# Revit family: R-CVA-0001
name_source: partatom
category: Fenêtres
units: mm (PartAtom-declared; Revit-internal decimal feet)

## family parameters
Couper avec des vides une fois chargée = Non
Hôte = Mur
Partagée = Non
Point de calcul de pièce = Non
Toujours verticalement = Oui

## types (2) — shared parameters
Acoustique = Rw (C ; Ctr) = 37 (-1 ; -3) dB
Anti-Effraction = RESISTANCE AUX CHOCS : 2B2 (900J) (selon NF EN 12600))
Applique = Non
Construction analytique = <Aucun>
Description = Chassis vitré, EW30, 37(-1; -3) dB (performance du vitrage), résistance aux chocs 2B2, sans résistance aux UV, avec parcloses bois, sur cadre bois
Fabricant = MONTIBERT
Fiche_Produit = CVA-0001
Huisserie_Delardage Largeur = 8 mm  [stored 0.0262467 ft]
Huisserie_Délardage Bas Epaisseur = 8 mm  [stored 0.0262467 ft]
Huisserie_Délardage Haut  Epaisseur = 8 mm  [stored 0.0262467 ft]
Huisserie_Délardage_Bas = Non
Huisserie_Délardage_Haut = Non
Huisserie_Feuillure Largeur = 24 mm  [stored 0.0787402 ft]
Huisserie_Feuillure_Basse = Non
Huisserie_Feuillure_Haute = Non
Huisserie_Feuillure_Sans = Oui
Huisserie_Matériau = Hêtre
Huisserie_Profil_Epaisseur = 118 mm  [stored 0.387139 ft]
Huisserie_Rainure à Brique_Largeur = 8 mm  [stored 0.0262467 ft]
Materiaux_Dominant = Bois
Modèle = 05 - Châssis Vitré
Montant_1 = Non
Montant_2 = Non
Montant_Largeur = 72 mm  [stored 0.23622 ft]
Note d'identification = CHASSIS VITRE EW30
Parclosage à Recouvrement = Non
Parclose Jeu Epaisseur = 1 mm  [stored 0.00328084 ft]
Parclose Largeur = 24 mm  [stored 0.0787402 ft]
Parclose Recouvrement Epaisseur = 6 mm  [stored 0.019685 ft]
Parclose Recouvrement Largeur = 6 mm  [stored 0.019685 ft]
Parcloses_Matériau = Hêtre
Profil 1_Largeur = 50 mm  [stored 0.164042 ft]
Profil 1_Latéral = Non
Profil 2_Largeur = 50 mm  [stored 0.164042 ft]
Profil 2_Latéral = Non
Profil Bas = Non
Profil Bas_Largeur = 70 mm  [stored 0.229659 ft]
Profil Haut = Non
Profil Haut_Largeur = 50 mm  [stored 0.164042 ft]
Profil_Délardage_Bas_Epaisseur = 8 mm  [stored 0.0262467 ft]
Profil_Délardage_Haut_Epaisseur = 8 mm  [stored 0.0262467 ft]
Profil_Délardage_Largeur = 8 mm  [stored 0.0262467 ft]
Profil_Matériau = Hêtre
Profil_Rainure à Brique_ coté Int = Oui
Profils_Délardage Bas_coté Ext = Non
Profils_Délardage Bas_coté Int = Non
Profils_Délardage Haut_coté Ext = Non
Profils_Délardage Haut_coté Int = Non
Profils_Déplacement X = 8 mm  [stored 0.0262467 ft]
Profils_Déplacement Y' = 8 mm  [stored 0.0262467 ft]
Reference_Commerciale = C EW30 VAc
Resistance_Feu = E30-EW130
Sens_Feu = Recto / Verso
URL = https://www.malerba.fr
Vitrage_Matériau = Verre
zero-valued in all types: Ambrasure, Jeu Bas, Jeu Haut, Jeu Latéral 1, Jeu Latéral 2, Parclose Jeu Largeur, Profils_Déplacement X', Profils_Déplacement Y, X3'_Déduction Délardages Profils, X3_Déduction Délardages Profils, X_Ambrasure, X_Huisserie Décalage Hauteur, X_Huisserie Décalage Hauteur_INV, X_Huisserie Décalage Largeur, X_Huisserie Décalage Largeur_INV, X_Profil 1_Largeur, X_Profil 2_Largeur, X_Profil Bas_Largeur, X_Profil Haut_Largeur

## per-type parameters (varying)
- CVA-0001: Châssis Hauteur Hors Tout=577 mm; Châssis Largeur Hors Tout=1141 mm  [stored 3.74344 ft]; Code_MAJ=2022012506CVA0001; Huisserie_Feuillure Epaisseur=33 mm  [stored 0.108268 ft]; Huisserie_Profil_Largeur=58 mm; Huisserie_Rainure à Brique=Oui; Profil_Déplacement Vers Nu Ext=Oui; Profil_Déplacement Vers Nu Int=Non; Profil_Déplacement Vers l'Huisserie=Non; Profil_Déplacement Vers le Mur=Oui; Profil_Rainure à Brique_ coté Ext=Oui; Recouvrement=Oui; Tunnel=Non; Vitrage Epaisseur=11 mm  [stored 0.0360892 ft]; X1'_Tunnel=577 mm; X1_Tunnel=1141 mm  [stored 3.74344 ft]; X2'_Recouvrement et Applique=561 mm  [stored 1.84055 ft]; X2_Recouvrement et Applique=1125 mm  [stored 3.69094 ft]; X4'_Déduction Délardages Huisseries=16 mm  [stored 0.0524934 ft]; X4_Déduction Délardages Huisseries=16 mm  [stored 0.0524934 ft]; X_Ambrasure Décalage Epaisseur=0 mm  [stored 0 ft]; X_Huisserie_Delardage Largeur=8 mm  [stored 0.0262467 ft]; X_Ouvertur Mur Largeur=1125 mm  [stored 3.69094 ft]; X_Ouverture Mur Hauteur=561 mm  [stored 1.84055 ft]; X_Profil_Délardage_Largeur=8 mm  [stored 0.0262467 ft]
- CVA-0001 579: Châssis Hauteur Hors Tout=579 mm; Châssis Largeur Hors Tout=1140 mm; Code_MAJ=2019102206CVA0001; Huisserie_Feuillure Epaisseur=40 mm  [stored 0.131234 ft]; Huisserie_Profil_Largeur=56 mm  [stored 0.183727 ft]; Huisserie_Rainure à Brique=Non; Profil_Déplacement Vers Nu Ext=Non; Profil_Déplacement Vers Nu Int=Oui; Profil_Déplacement Vers l'Huisserie=Oui; Profil_Déplacement Vers le Mur=Non; Profil_Rainure à Brique_ coté Ext=Non; Recouvrement=Non; Tunnel=Oui; Vitrage Epaisseur=16 mm  [stored 0.0524934 ft]; X1'_Tunnel=579 mm; X1_Tunnel=1140 mm; X2'_Recouvrement et Applique=579 mm; X2_Recouvrement et Applique=1140 mm; X4'_Déduction Délardages Huisseries=0 mm  [stored 0 ft]; X4_Déduction Délardages Huisseries=0 mm  [stored 0 ft]; X_Ambrasure Décalage Epaisseur=8 mm  [stored 0.0262467 ft]; X_Huisserie_Delardage Largeur=0 mm  [stored 0 ft]; X_Ouvertur Mur Largeur=1140 mm; X_Ouverture Mur Hauteur=579 mm; X_Profil_Délardage_Largeur=0 mm  [stored 0 ft]

note: [stored X ft] marks values corroborated as IEEE doubles in the binary element streams (Revit-internal decimal feet)

## geometry (parser evidence)
native form markers: Blend x24
no freeform markers — native parametric forms only
